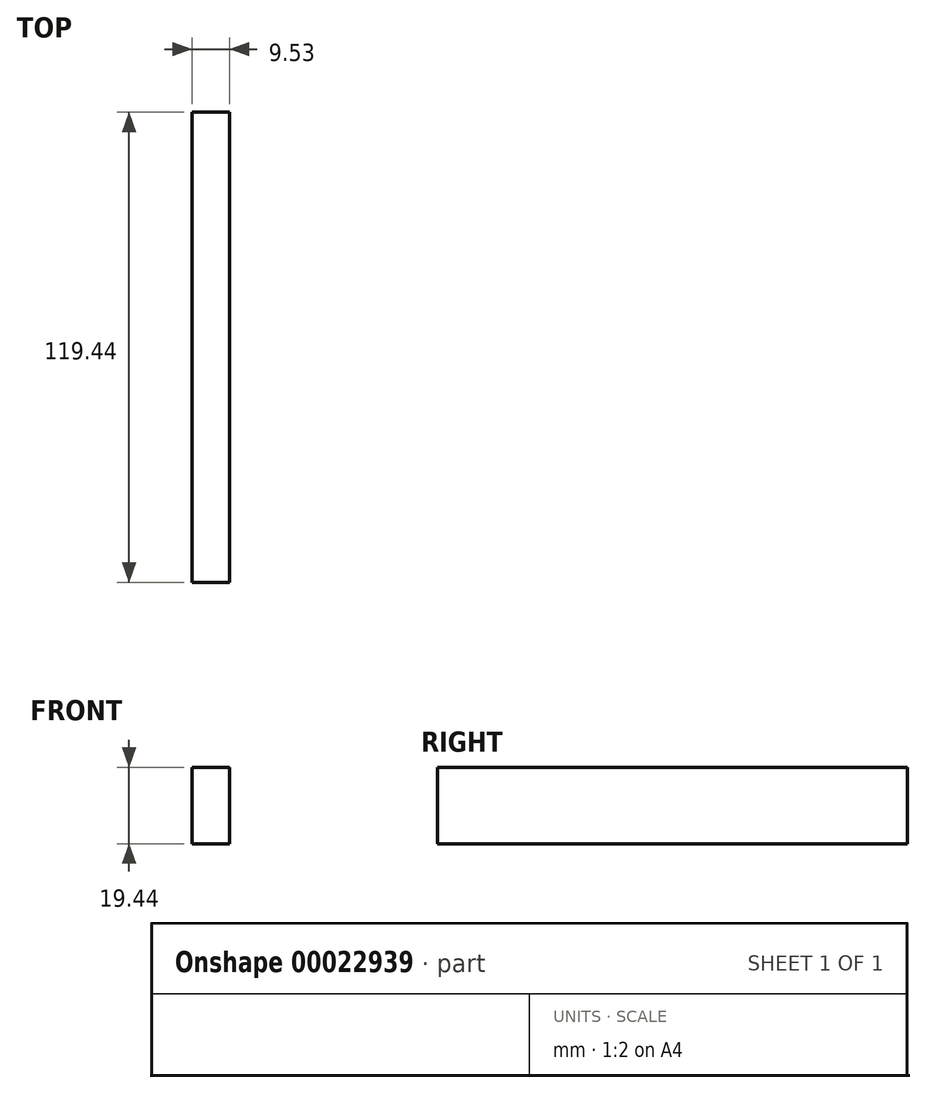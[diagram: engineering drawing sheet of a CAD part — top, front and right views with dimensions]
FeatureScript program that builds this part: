
annotation { "Feature Type Name" : "Feature", "Feature Type Description" : "" }
export const myFeature = defineFeature(function(context is Context, id is Id, definition is map)
    precondition{}
    {
        {
            var Q0;
            Q0=qCreatedBy(makeId("Right.planeOp"),FACE);
            var sketch = newSketch(context, id + "F0", { "sketchPlane" : qUnion([Q0])});
            skLineSegment(sketch, "E0.bottom", {"start": v(-63.42, 43.86) * mm, "end": v(56.02, 43.86) * mm});
            skLineSegment(sketch, "E0.top", {"start": v(-63.42, 24.42) * mm, "end": v(56.02, 24.42) * mm});
            skLineSegment(sketch, "E0.left", {"start": v(-63.42, 43.86) * mm, "end": v(-63.42, 24.42) * mm});
            skLineSegment(sketch, "E0.right", {"start": v(56.02, 43.86) * mm, "end": v(56.02, 24.42) * mm});
            skSolve(sketch);
        }
        {
            var Q0;
            Q0=makeQuery(id+"F0.imprint","IMPRINT",FACE,{"disambiguationData":[TD([[makeQuery(id+"F0.imprint","IMPRINT",EDGE,{"derivedFrom":sQuery(id+"F0.wireOp",EDGE,"E0.bottom")}),-1.0]])]});
            extrude(context, id + "F1", {"entities" : qUnion([Q0]), "depth" : 9.52 * mm});
        }
    });
